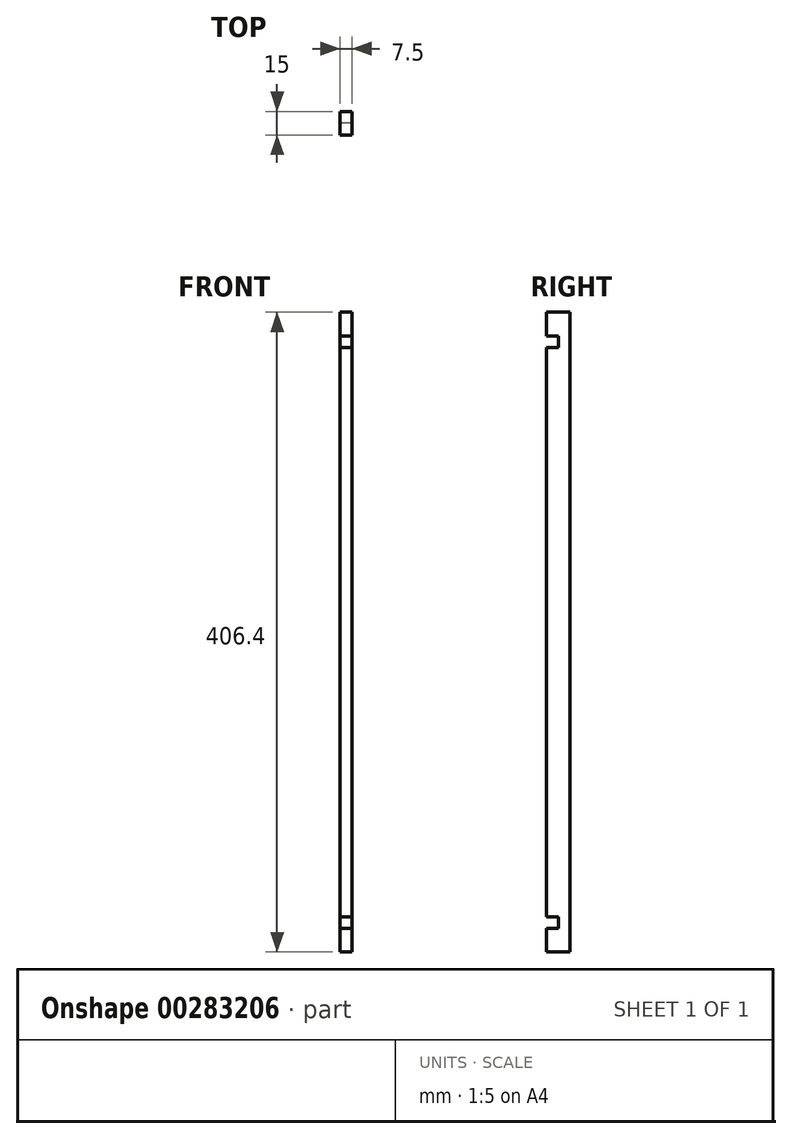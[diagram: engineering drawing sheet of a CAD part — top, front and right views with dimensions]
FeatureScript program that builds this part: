
annotation { "Feature Type Name" : "Feature", "Feature Type Description" : "" }
export const myFeature = defineFeature(function(context is Context, id is Id, definition is map)
    precondition{}
    {
        {
            var Q0;
            Q0=qCreatedBy(makeId("Right.planeOp"),FACE);
            var sketch = newSketch(context, id + "F0", { "sketchPlane" : qUnion([Q0])});
            skLineSegment(sketch, "E0.bottom", {"start": v(7.5, 203.2) * mm, "end": v(-7.5, 203.2) * mm});
            skLineSegment(sketch, "E0.top", {"start": v(7.5, -203.2) * mm, "end": v(-7.5, -203.2) * mm});
            skLineSegment(sketch, "E0.left", {"start": v(7.5, 203.2) * mm, "end": v(7.5, -203.2) * mm});
            skLineSegment(sketch, "E0.right", {"start": v(-7.5, 203.2) * mm, "end": v(-7.5, 188.2) * mm});
            skPoint(sketch, "E0.middle", {"position": v(0, 0) * mm});
            skLineSegment(sketch, "E1", {"start": v(0, -203.2) * mm, "end": v(0, -188.2) * mm, "construction": true});
            skPoint(sketch, "E1.endSnap0", {"position": v(0, -203.2) * mm});
            skLineSegment(sketch, "E2", {"start": v(0, 203.2) * mm, "end": v(0, 188.2) * mm, "construction": true});
            skPoint(sketch, "E2.endSnap0", {"position": v(0, 203.2) * mm});
            skLineSegment(sketch, "E3.bottom", {"start": v(-7.5, -188.2) * mm, "end": v(0, -188.2) * mm});
            skLineSegment(sketch, "E3.top", {"start": v(-7.5, -180.7) * mm, "end": v(0, -180.7) * mm});
            skLineSegment(sketch, "E3.right", {"start": v(0, -188.2) * mm, "end": v(0, -180.7) * mm});
            skLineSegment(sketch, "E4.bottom", {"start": v(0, 188.2) * mm, "end": v(-7.5, 188.2) * mm});
            skLineSegment(sketch, "E4.top", {"start": v(0, 180.7) * mm, "end": v(-7.5, 180.7) * mm});
            skLineSegment(sketch, "E4.left", {"start": v(0, 188.2) * mm, "end": v(0, 180.7) * mm});
            skLineSegment(sketch, "E5.trimOffspring", {"start": v(-7.5, 180.7) * mm, "end": v(-7.5, -180.7) * mm});
            skLineSegment(sketch, "E6.trimOffspring", {"start": v(-7.5, -188.2) * mm, "end": v(-7.5, -203.2) * mm});
            skSolve(sketch);
        }
        {
            var Q0;
            Q0=makeQuery(id+"F0.imprint","IMPRINT",FACE,{"disambiguationData":[TD([[makeQuery(id+"F0.imprint","IMPRINT",EDGE,{"derivedFrom":sQuery(id+"F0.wireOp",EDGE,"E0.bottom")}),1.0]])]});
            extrude(context, id + "F1", {"entities" : qUnion([Q0]), "endBound" : BoundingType.SYMMETRIC, "depth" : 7.5 * mm});
        }
    });
